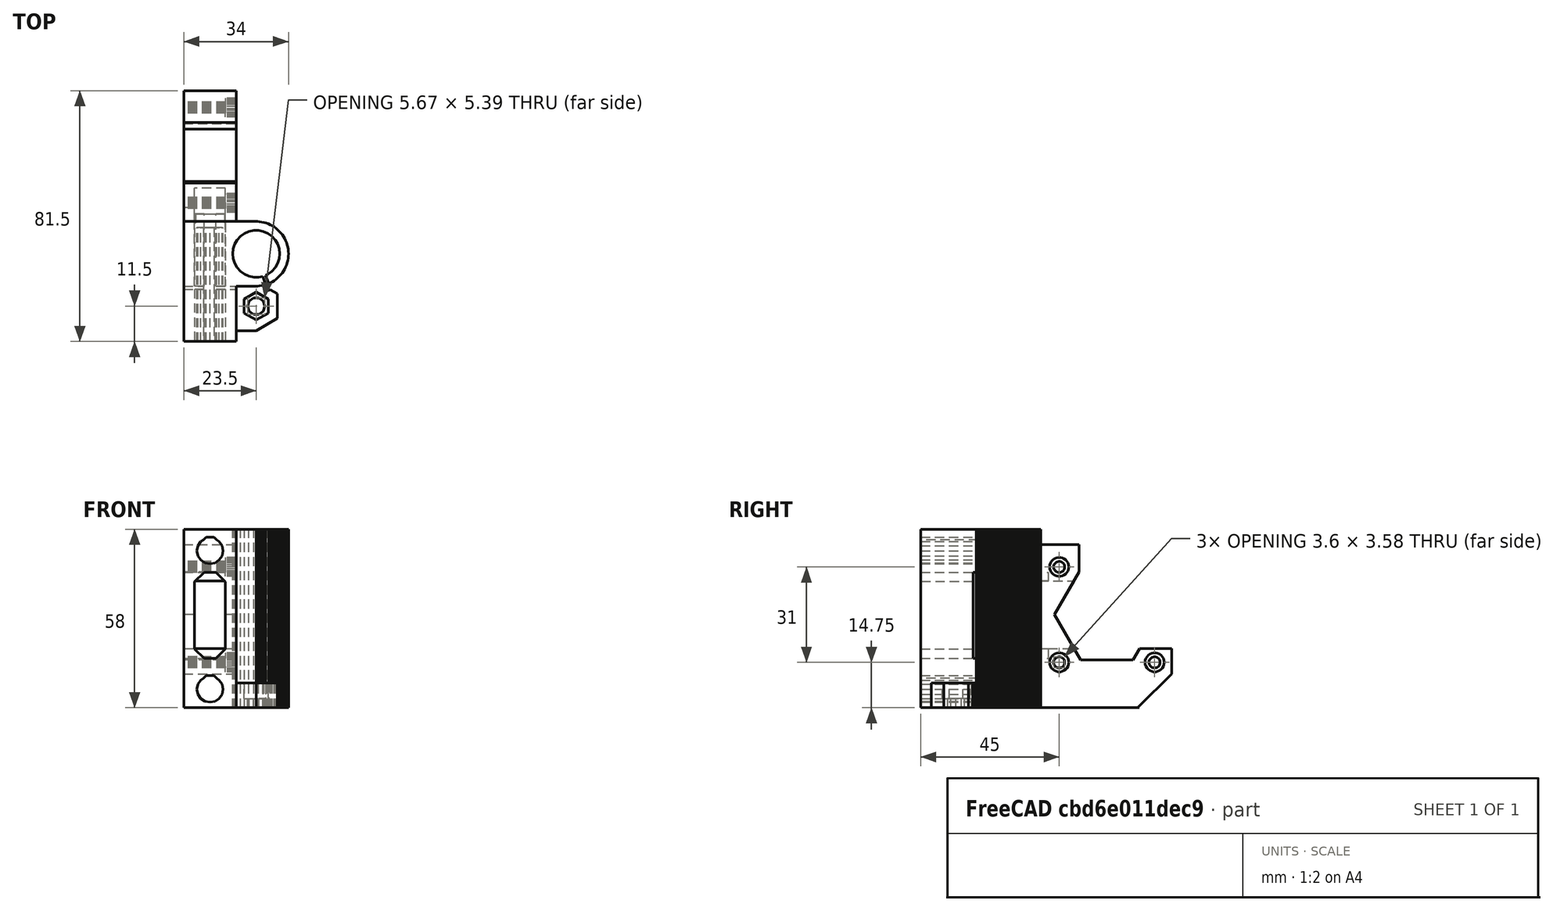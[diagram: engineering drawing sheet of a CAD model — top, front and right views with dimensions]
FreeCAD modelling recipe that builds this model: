
FCSTD DOCUMENT  (FreeCAD 0.15R4368 (Git))
Label: x-end-motor
License: CC-BY 3.0
LicenseURL: http://creativecommons.org/licenses/by/3.0/
objects: Part::Box×18, Part::Prism×16, Part::Fuse×7, Part::MultiFuse×4, Part::Cut×4, Part::Feature×1
note: 50 computed .brp shape members not serialized (recipe doc carries the construction recipe); baked Part::Feature solids carry a one-line shape summary decoded from their .brp

FEATURE [Part::Box] cube
  Height = 58
  Length = 17
  Placement = pos=(-23.5,-28.5,0) rot=(0,0,1;0rad)
  Width = 39
FEATURE [Part::Box] cube001
  Height = 58
  Length = 14.5
  Placement = pos=(-14.5,-10.5,0) rot=(0,0,1;0rad)
  Width = 21
FEATURE [Part::Prism] prism
  Circumradius = 10.5
  Height = 58
  Polygon = 90
FEATURE [Part::Fuse] Group
  Base = -> cube001
  Tool = -> prism
FEATURE [Part::Box] cube002
  Height = 8
  Length = 8
  Placement = pos=(-8,-25,0) rot=(0,0,1;0rad)
  Width = 16
FEATURE [Part::Prism] prism001
  Circumradius = 8
  Height = 8
  Placement = pos=(0,-17,0) rot=(0,0,1;0.523599rad)
  Polygon = 6
FEATURE [Part::MultiFuse] Group001
  Shapes = -> [cube,Group,cube002,prism001]
FEATURE [Part::Box] cube003
  Height = 53
  Length = 17
  Placement = pos=(-23.5,9,0) rot=(0,0,1;0rad)
  Width = 44
FEATURE [Part::Fuse] Group002
  Base = -> Group001
  Tool = -> cube003
FEATURE [Part::Prism] prism002
  Circumradius = 7.64131
  Height = 62
  Placement = pos=(0,0,-1) rot=(0,0,1;0rad)
  Polygon = 30
FEATURE [Part::Box] cube004
  Height = 62
  Length = 6
  Placement = pos=(1.75328,-6.27901,-1) rot=(0,0,-1;1.22173rad)
  Width = 1
FEATURE [Part::Fuse] Group003
  Base = -> prism002
  Tool = -> cube004
FEATURE [Part::Box] cube005
  Height = 28
  Length = 20
  Placement = pos=(-24,-11.5,16) rot=(0,0,1;0rad)
  Width = 1
FEATURE [Part::Box] cube006
  Height = 28
  Length = 10
  Placement = pos=(-19,-33,16) rot=(0,0,1;0rad)
  Width = 46
FEATURE [Part::Box] cube007
  Height = 28
  Length = 10
  Placement = pos=(-27.435,-33,46.636) rot=(0,1,0;0.785398rad)
  Width = 46
FEATURE [Part::Box] cube008
  Height = 28
  Length = 10
  Placement = pos=(-7.63604,-33,39.565) rot=(0,-1,0;0.785398rad)
  Width = 46
FEATURE [Part::Box] cube009
  Height = 28
  Length = 10
  Placement = pos=(-27.435,-33,0.636039) rot=(0,1,0;0.785398rad)
  Width = 46
FEATURE [Part::Box] cube010
  Height = 28
  Length = 10
  Placement = pos=(-7.63604,-33,-6.43503) rot=(0,-1,0;0.785398rad)
  Width = 46
FEATURE [Part::MultiFuse] union
  Shapes = -> [cube007,cube008,cube009,cube010]
FEATURE [Part::Cut] difference
  Base = -> cube006
  Tool = -> union
FEATURE [Part::Fuse] Matrix_Union
  Base = -> cube005
  Placement = pos=(-1,0,0) rot=(0,0,1;0rad)
  Tool = -> difference
FEATURE [Part::Prism] prism003
  Circumradius = 4.22934
  Height = 50
  Polygon = 16
FEATURE [Part::Box] cube011
  Height = 50
  Length = 4.05
  Placement = pos=(0,-5.70589,0) rot=(0,0,1;0.785398rad)
  Width = 4.05
FEATURE [Part::Box] cube012
  Height = 50
  Length = 8.1
  Placement = pos=(-4.05,-8.5,0) rot=(0,0,1;0rad)
  Width = 4.05
FEATURE [Part::Cut] difference001
  Base = -> cube011
  Tool = -> cube012
FEATURE [Part::Fuse] Group004
  Base = -> prism003
  Placement = pos=(-15,-41.5,6) rot=(-1,0,0;1.5708rad)
  Tool = -> difference001
FEATURE [Part::Prism] prism004
  Circumradius = 4.22934
  Height = 50
  Polygon = 16
FEATURE [Part::Box] cube013
  Height = 50
  Length = 4.05
  Placement = pos=(0,-5.70589,0) rot=(0,0,1;0.785398rad)
  Width = 4.05
FEATURE [Part::Box] cube014
  Height = 50
  Length = 8.1
  Placement = pos=(-4.05,-8.5,0) rot=(0,0,1;0rad)
  Width = 4.05
FEATURE [Part::Cut] difference002
  Base = -> cube013
  Tool = -> cube014
FEATURE [Part::Fuse] Group005
  Base = -> prism004
  Placement = pos=(-15,-41.5,51) rot=(-1,0,0;1.5708rad)
  Tool = -> difference002
FEATURE [Part::Prism] prism005
  Circumradius = 2.8338
  Height = 4
  Placement = pos=(0,-17,-0.5) rot=(0,0,1;0rad)
  Polygon = 10
FEATURE [Part::Prism] prism006
  Circumradius = 4.5
  Height = 10
  Placement = pos=(0,-17,3) rot=(0,0,1;0.523599rad)
  Polygon = 6
FEATURE [Part::MultiFuse] Group006
  Shapes = -> [Group003,Matrix_Union,Group004,Group005,prism005,prism006]
FEATURE [Part::Box] cube015
  Height = 22
  Length = 10
  Placement = pos=(-19,-22,-11) rot=(0,0,1;0rad)
  Width = 46
FEATURE [Part::Prism] prism007
  Circumradius = 1.8
  Height = 70
  Placement = pos=(20,-15.5,-15.5) rot=(-0.57735,-0.57735,0.57735;2.0944rad)
  Polygon = 30
FEATURE [Part::Prism] prism008
  Circumradius = 3.1
  Height = 10
  Placement = pos=(1,-15.5,-15.5) rot=(-0.57735,-0.57735,0.57735;2.0944rad)
  Polygon = 30
FEATURE [Part::Prism] prism009
  Circumradius = 1.8
  Height = 70
  Placement = pos=(20,-15.5,15.5) rot=(-0.57735,-0.57735,0.57735;2.0944rad)
  Polygon = 30
FEATURE [Part::Prism] prism010
  Circumradius = 3.1
  Height = 10
  Placement = pos=(1,-15.5,15.5) rot=(-0.57735,-0.57735,0.57735;2.0944rad)
  Polygon = 30
FEATURE [Part::Prism] prism011
  Circumradius = 1.8
  Height = 70
  Placement = pos=(20,15.5,-15.5) rot=(-0.57735,-0.57735,0.57735;2.0944rad)
  Polygon = 30
FEATURE [Part::Prism] prism012
  Circumradius = 3.1
  Height = 10
  Placement = pos=(1,15.5,-15.5) rot=(-0.57735,-0.57735,0.57735;2.0944rad)
  Polygon = 30
FEATURE [Part::Prism] prism013
  Circumradius = 1.8
  Height = 70
  Placement = pos=(20,15.5,15.5) rot=(-0.57735,-0.57735,0.57735;2.0944rad)
  Polygon = 30
FEATURE [Part::Prism] prism014
  Circumradius = 3.1
  Height = 10
  Placement = pos=(1,15.5,15.5) rot=(-0.57735,-0.57735,0.57735;2.0944rad)
  Polygon = 30
FEATURE [Part::Box] cube016
  Height = 42
  Length = 60
  Placement = pos=(-40,-9,-11) rot=(0,0,1;0rad)
  Width = 42
FEATURE [Part::Box] cube017
  Height = 42
  Length = 60
  Placement = pos=(-40,40,-59.6985) rot=(1,0,0;0.785398rad)
  Width = 42
FEATURE [Part::Prism] prism015
  Circumradius = 17
  Height = 70
  Placement = pos=(0,0,0) rot=(-0.57735,-0.57735,0.57735;2.0944rad)
  Polygon = 6
FEATURE [Part::MultiFuse] Matrix_Union001
  Placement = pos=(-1,32,30.25) rot=(0,0,1;0rad)
  Shapes = -> [cube015,prism007,prism008,prism009,prism010,prism011,prism012,prism013,prism014,cube016,cube017,prism015]
FEATURE [Part::Fuse] Group007
  Base = -> Group006
  Tool = -> Matrix_Union001
FEATURE [Part::Cut] difference003
  Base = -> Group002
  Tool = -> Group007
FEATURE [Part::Feature] difference003001  label="XmotorPrusa"
  shape: bbox 34 x 81.5 x 58 mm, 364 faces (baked)
